# Revit family: NLRS_31_WI_WB_HS42R wandelement-AV_jazo_jazo
name_source: partatom
category: Windows
units: mm (PartAtom-declared; Revit-internal decimal feet)

## family parameters
Always vertical = Yes
Cut with Voids When Loaded = No
Host = Wall
OmniClass Number = 23.30.20.00
OmniClass Title = Windows
Room Calculation Point = No
Shared = No

## types (1)
- TYPE CATALOG
    Analytic Construction = <None>
    Assembly Code = 23.30.20.00
    Construction Type = Voor specificaties of mogelijkheden, neem contact op.
    Define Thermal Properties by = Schematic Type
    Description = HS42R wandelement
    Height = 1500 mm  [stored 4.92126 ft]
    JAZO_C_aluminium kozijn = No
    JAZO_C_forster presto kozijn = Yes
    JAZO_C_materiaal aluminium kozijn = <By Category>
    JAZO_C_materiaal aluminium planken = <By Category>
    JAZO_C_materiaal forster presto kozijn = <By Category>
    JAZO_C_materiaal forster presto sandwichpaneel = <By Category>
    JAZO_C_materiaal schoep = <By Category>
    JAZO_C_niet ventilerend = Yes
    JAZO_C_opbouwrooster HS42R = Yes
    JAZO_C_ventilerend = No
    MAX HEIGHT = 3000 mm  [stored 9.84252 ft]
    MAX WIDTH = 2800 mm  [stored 9.18635 ft]
    MIN HEIGHT = 300 mm
    MIN WIDTH = 440 mm  [stored 1.44357 ft]
    Manufacturer = JAZO Zevenaar bv
    Model = HS42R wandelement
    NLRS_C_aantal_01 = 29
    NLRS_C_brandwerend = No
    NLRS_C_breedte = 1500 mm  [stored 4.92126 ft]
    NLRS_C_breedte_01 = 1510 mm  [stored 4.95407 ft]
    NLRS_C_breedte_02 = 1452 mm  [stored 4.76378 ft]
    NLRS_C_breedte_max = 2800 mm  [stored 9.18635 ft]
    NLRS_C_breedte_min = 440 mm  [stored 1.44357 ft]
    NLRS_C_content_datum gewijzigd = 30-8-2022
    NLRS_C_content_datum uitgifte = 17-8-2022
    NLRS_C_content_provider = JAZO Zevenaar bv
    NLRS_C_content_revit versie = 2020.2
    NLRS_C_content_versie = 1.1
    NLRS_C_diepte = 50 mm  [stored 0.164042 ft]
    NLRS_C_geluidwering Rw = Voor specificaties of mogelijkheden, neem contact op.
    NLRS_C_hoogte = 1500 mm  [stored 4.92126 ft]
    NLRS_C_hoogte_01 = 1510 mm  [stored 4.95407 ft]
    NLRS_C_hoogte_02 = 1452 mm  [stored 4.76378 ft]
    NLRS_C_hoogte_max = 3000 mm  [stored 9.84252 ft]
    NLRS_C_hoogte_min = 300 mm
    NLRS_C_inbraakwerend = No
    NLRS_C_leverancier_adres = Handelsdwarsstraat 10
    NLRS_C_leverancier_bedrijfsnaam = JAZO Zevenaar bv
    NLRS_C_leverancier_plaats = Zevenaar
    NLRS_C_leverancier_postcode = 6905 DJ
    NLRS_C_leverancier_telefoonnummer = +31 316 - 59 29 11
    NLRS_C_leverancier_url = www.jazo.com
    NLRS_C_merk = Voor specificaties of mogelijkheden, neem contact op.
    NLRS_C_offset = 61 mm  [stored 0.200131 ft]
    NLRS_C_rookwerendheid = Voor specificaties of mogelijkheden, neem contact op.
    NLRS_C_stelruimte = 5 mm  [stored 0.0164042 ft]
    NLRS_C_weerstandsklasse = Voor specificaties of mogelijkheden, neem contact op.
    Negge = 61 mm  [stored 0.200131 ft]
    Rough Height = 1510 mm  [stored 4.95407 ft]
    Rough Width = 1510 mm  [stored 4.95407 ft]
    Thickness = 50 mm  [stored 0.164042 ft]
    URL = www.jazo.com
    Wall Closure = By host
    Width = 1500 mm  [stored 4.92126 ft]

note: [stored X ft] marks values corroborated as IEEE doubles in the binary element streams (Revit-internal decimal feet)

## geometry (parser evidence)
native form markers: Sweep x20
no freeform markers — native parametric forms only
